# Revit family: duet 06-19-2017
name_source: partatom
category: Lighting Fixtures
revit_build: Autodesk Revit 2014 (Build: 20130308_1515(x64)
units: mm (PartAtom-declared; Revit-internal decimal feet)

## types (5) — shared parameters
1 module visibility = No
normal visibility = Yes
rotation = 0.00°

## per-type parameters (varying)
| type | 2nd array | Modules Numbers | a | a/2 | array length | array number | led module length |
| LeeSti Duet 1' | 7 | 7 | 1' - 1 29/32" | 0' - 6 15/16" | 8' - 1 9/32" | 8 | 1' - 0 1/2" |
| LeeSti Duet 2' | 7 | 7 | 2' - 0 29/32" | 1' - 0 7/16" | 14' - 6 9/32" | 8 | 1' - 11 1/2" |
| Leesti Duet 3' | 7 | 7 | 3' - 0 13/32" | 1' - 6 3/16" | 21' - 2 25/32" | 8 | 2' - 11" |
| Leesti Duet 4' | 2 | 2 | 3' - 11 13/32" | 1' - 11 11/16" | 7' - 10 13/16" | 3 | 3' - 10" |
| Leesti Duet 8' | 7 | 7 | 7' - 9 13/32" | 3' - 10 11/16" | 54' - 5 25/32" | 8 | 7' - 8" |

## geometry (parser evidence)
native form markers: Sweep x15
no freeform markers — native parametric forms only
